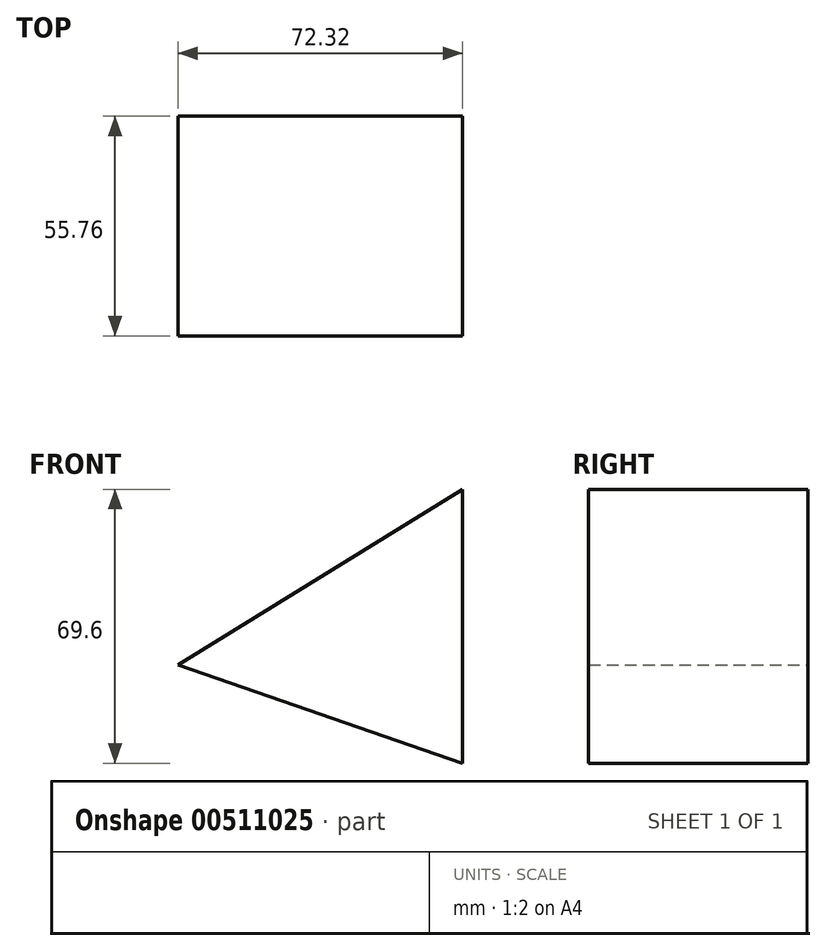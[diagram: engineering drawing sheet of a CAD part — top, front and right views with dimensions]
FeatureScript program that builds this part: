
annotation { "Feature Type Name" : "Feature", "Feature Type Description" : "" }
export const myFeature = defineFeature(function(context is Context, id is Id, definition is map)
    precondition{}
    {
        {
            var Q0;
            Q0=qCreatedBy(makeId("Front.planeOp"),FACE);
            var sketch = newSketch(context, id + "F0", { "sketchPlane" : qUnion([Q0])});
            skLineSegment(sketch, "E0", {"start": v(43.8, 44.64) * mm, "end": v(43.8, -24.96) * mm});
            skLineSegment(sketch, "E1", {"start": v(43.8, -24.96) * mm, "end": v(-28.52, 0) * mm});
            skLineSegment(sketch, "E2", {"start": v(-28.52, 0) * mm, "end": v(43.8, 44.64) * mm});
            skSolve(sketch);
        }
        {
            var Q0;
            Q0=makeQuery(id+"F0.imprint","IMPRINT",FACE,{"disambiguationData":[TD([[makeQuery(id+"F0.imprint","IMPRINT",EDGE,{"derivedFrom":sQuery(id+"F0.wireOp",EDGE,"E0")}),-1.0]])]});
            extrude(context, id + "F1", {"entities" : qUnion([Q0]), "depth" : 55.76 * mm});
        }
    });
